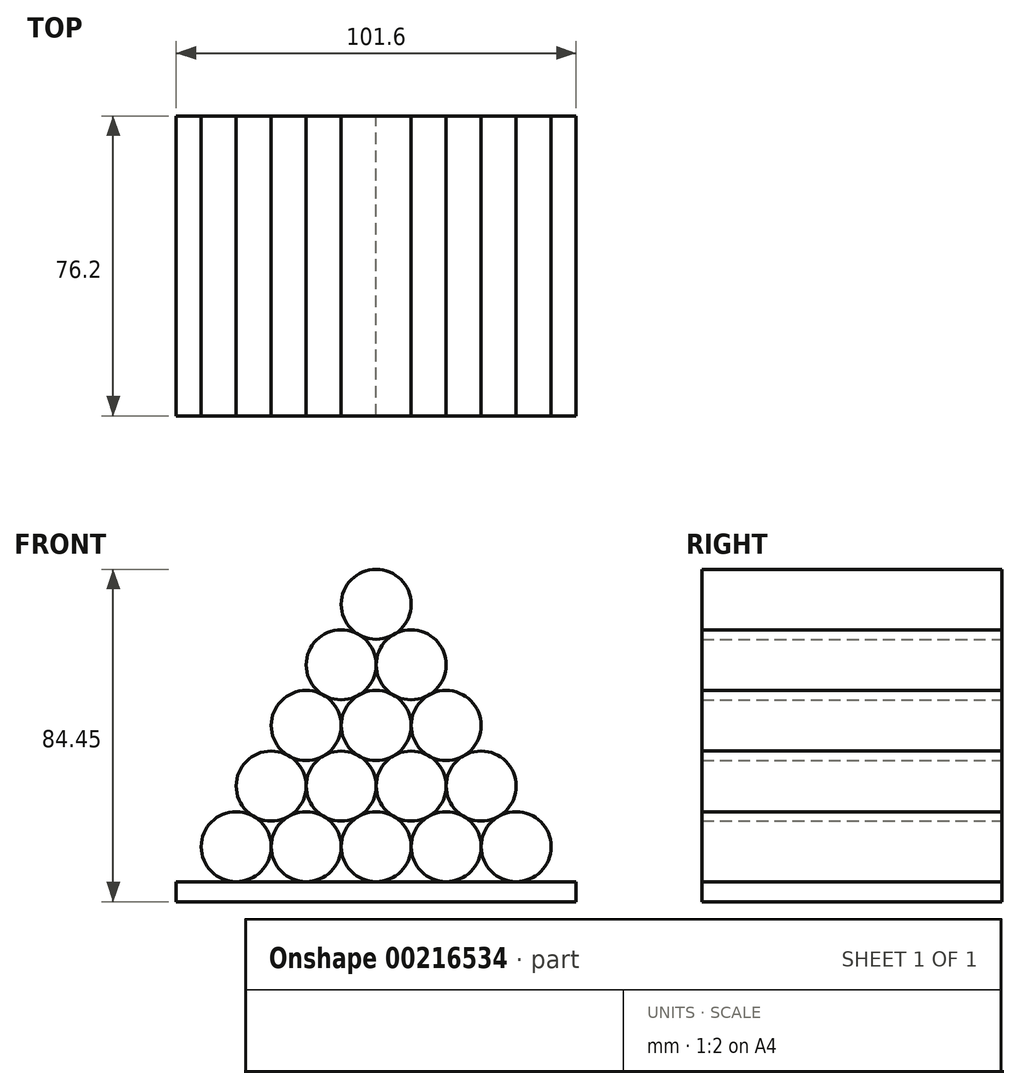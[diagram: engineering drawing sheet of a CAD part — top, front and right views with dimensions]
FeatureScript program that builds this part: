
annotation { "Feature Type Name" : "Feature", "Feature Type Description" : "" }
export const myFeature = defineFeature(function(context is Context, id is Id, definition is map)
    precondition{}
    {
        {
            var Q0;
            Q0=qCreatedBy(makeId("Front.planeOp"),FACE);
            var sketch = newSketch(context, id + "F0", { "sketchPlane" : qUnion([Q0])});
            skCircle(sketch, "E0", {"center": v(-26.67, 0) * mm, "radius": 8.9 * mm});
            skCircle(sketch, "E1", {"center": v(-8.9, 0) * mm, "radius": 8.9 * mm});
            skCircle(sketch, "E2", {"center": v(8.9, 0) * mm, "radius": 8.9 * mm});
            skCircle(sketch, "E3", {"center": v(26.67, 0) * mm, "radius": 8.9 * mm});
            skCircle(sketch, "E4", {"center": v(-17.78, 15.4) * mm, "radius": 8.9 * mm});
            skCircle(sketch, "E5", {"center": v(0, 15.4) * mm, "radius": 8.9 * mm});
            skCircle(sketch, "E6", {"center": v(17.78, 15.4) * mm, "radius": 8.9 * mm});
            skCircle(sketch, "E7", {"center": v(-35.56, -15.4) * mm, "radius": 8.9 * mm});
            skCircle(sketch, "E8", {"center": v(-17.78, -15.4) * mm, "radius": 8.9 * mm});
            skCircle(sketch, "E9", {"center": v(0, -15.4) * mm, "radius": 8.9 * mm});
            skCircle(sketch, "E10", {"center": v(17.78, -15.4) * mm, "radius": 8.9 * mm});
            skCircle(sketch, "E11", {"center": v(35.56, -15.4) * mm, "radius": 8.9 * mm});
            skLineSegment(sketch, "E12.bottom", {"start": v(-50.8, -24.29) * mm, "end": v(50.8, -24.29) * mm});
            skLineSegment(sketch, "E12.top", {"start": v(-50.8, -29.37) * mm, "end": v(50.8, -29.37) * mm});
            skLineSegment(sketch, "E12.left", {"start": v(-50.8, -24.29) * mm, "end": v(-50.8, -29.37) * mm});
            skLineSegment(sketch, "E12.right", {"start": v(50.8, -24.29) * mm, "end": v(50.8, -29.37) * mm});
            skCircle(sketch, "E13", {"center": v(-8.9, 30.8) * mm, "radius": 8.9 * mm});
            skCircle(sketch, "E14", {"center": v(8.89, 30.8) * mm, "radius": 8.9 * mm});
            skCircle(sketch, "E15", {"center": v(0, 46.2) * mm, "radius": 8.9 * mm});
            skSolve(sketch);
        }
        {
            var Q0;
            {var subQ0=sQuery(id+"F0.wireOp",EDGE,"E4");var subQ1=makeQuery(id+"F0.imprint","INTERSECT",VERTEX,{"derivedFrom":[sQuery(id+"F0.wireOp",EDGE,"E0"),subQ0]});Q0=makeQuery(id+"F0.imprint","IMPRINT",FACE,{"disambiguationData":[TD([[makeQuery(id+"F0.imprint","IMPRINT",EDGE,{"disambiguationData":[TD([[subQ1,1.0]])],"derivedFrom":subQ0}),1.0]])]});}
            var Q1;
            {var subQ0=sQuery(id+"F0.wireOp",EDGE,"E5");var subQ1=makeQuery(id+"F0.imprint","INTERSECT",VERTEX,{"derivedFrom":[sQuery(id+"F0.wireOp",EDGE,"E4"),subQ0]});Q1=makeQuery(id+"F0.imprint","IMPRINT",FACE,{"disambiguationData":[TD([[makeQuery(id+"F0.imprint","IMPRINT",EDGE,{"disambiguationData":[TD([[subQ1,1.0]])],"derivedFrom":subQ0}),1.0]])]});}
            var Q2;
            {var subQ0=sQuery(id+"F0.wireOp",EDGE,"E6");var subQ1=makeQuery(id+"F0.imprint","INTERSECT",VERTEX,{"derivedFrom":[sQuery(id+"F0.wireOp",EDGE,"E5"),subQ0]});Q2=makeQuery(id+"F0.imprint","IMPRINT",FACE,{"disambiguationData":[TD([[makeQuery(id+"F0.imprint","IMPRINT",EDGE,{"disambiguationData":[TD([[subQ1,-1.0]])],"derivedFrom":subQ0}),1.0]])]});}
            var Q3;
            {var subQ0=sQuery(id+"F0.wireOp",EDGE,"E3");var subQ1=makeQuery(id+"F0.imprint","INTERSECT",VERTEX,{"derivedFrom":[subQ0,sQuery(id+"F0.wireOp",EDGE,"E6")]});Q3=makeQuery(id+"F0.imprint","IMPRINT",FACE,{"disambiguationData":[TD([[makeQuery(id+"F0.imprint","IMPRINT",EDGE,{"disambiguationData":[TD([[subQ1,-1.0]])],"derivedFrom":subQ0}),1.0]])]});}
            var Q4;
            {var subQ0=sQuery(id+"F0.wireOp",EDGE,"E2");var subQ4=makeQuery(id+"F0.imprint","INTERSECT",VERTEX,{"derivedFrom":[subQ0,sQuery(id+"F0.wireOp",EDGE,"E6")]});Q4=makeQuery(id+"F0.imprint","IMPRINT",FACE,{"disambiguationData":[TD([[makeQuery(id+"F0.imprint","IMPRINT",EDGE,{"disambiguationData":[TD([[subQ4,1.0]])],"derivedFrom":subQ0}),1.0]])]});}
            var Q5;
            {var subQ0=sQuery(id+"F0.wireOp",EDGE,"E1");var subQ4=makeQuery(id+"F0.imprint","INTERSECT",VERTEX,{"derivedFrom":[subQ0,sQuery(id+"F0.wireOp",EDGE,"E5")]});Q5=makeQuery(id+"F0.imprint","IMPRINT",FACE,{"disambiguationData":[TD([[makeQuery(id+"F0.imprint","IMPRINT",EDGE,{"disambiguationData":[TD([[subQ4,1.0]])],"derivedFrom":subQ0}),1.0]])]});}
            var Q6;
            {var subQ0=sQuery(id+"F0.wireOp",EDGE,"E0");var subQ1=makeQuery(id+"F0.imprint","INTERSECT",VERTEX,{"derivedFrom":[subQ0,sQuery(id+"F0.wireOp",EDGE,"E4")]});Q6=makeQuery(id+"F0.imprint","IMPRINT",FACE,{"disambiguationData":[TD([[makeQuery(id+"F0.imprint","IMPRINT",EDGE,{"disambiguationData":[TD([[subQ1,1.0]])],"derivedFrom":subQ0}),1.0]])]});}
            var Q7;
            {var subQ0=sQuery(id+"F0.wireOp",EDGE,"E7");var subQ1=makeQuery(id+"F0.imprint","INTERSECT",VERTEX,{"derivedFrom":[sQuery(id+"F0.wireOp",EDGE,"E0"),subQ0]});Q7=makeQuery(id+"F0.imprint","IMPRINT",FACE,{"disambiguationData":[TD([[makeQuery(id+"F0.imprint","IMPRINT",EDGE,{"disambiguationData":[TD([[subQ1,1.0]])],"derivedFrom":subQ0}),1.0]])]});}
            var Q8;
            {var subQ0=sQuery(id+"F0.wireOp",EDGE,"E8");var subQ4=makeQuery(id+"F0.imprint","INTERSECT",VERTEX,{"derivedFrom":[sQuery(id+"F0.wireOp",EDGE,"E1"),subQ0]});Q8=makeQuery(id+"F0.imprint","IMPRINT",FACE,{"disambiguationData":[TD([[makeQuery(id+"F0.imprint","IMPRINT",EDGE,{"disambiguationData":[TD([[subQ4,1.0]])],"derivedFrom":subQ0}),1.0]])]});}
            var Q9;
            {var subQ0=sQuery(id+"F0.wireOp",EDGE,"E9");var subQ4=makeQuery(id+"F0.imprint","INTERSECT",VERTEX,{"derivedFrom":[sQuery(id+"F0.wireOp",EDGE,"E2"),subQ0]});Q9=makeQuery(id+"F0.imprint","IMPRINT",FACE,{"disambiguationData":[TD([[makeQuery(id+"F0.imprint","IMPRINT",EDGE,{"disambiguationData":[TD([[subQ4,1.0]])],"derivedFrom":subQ0}),1.0]])]});}
            var Q10;
            {var subQ0=sQuery(id+"F0.wireOp",EDGE,"E10");var subQ4=makeQuery(id+"F0.imprint","INTERSECT",VERTEX,{"derivedFrom":[sQuery(id+"F0.wireOp",EDGE,"E3"),subQ0]});Q10=makeQuery(id+"F0.imprint","IMPRINT",FACE,{"disambiguationData":[TD([[makeQuery(id+"F0.imprint","IMPRINT",EDGE,{"disambiguationData":[TD([[subQ4,1.0]])],"derivedFrom":subQ0}),1.0]])]});}
            var Q11;
            {var subQ0=sQuery(id+"F0.wireOp",EDGE,"E11");var subQ1=makeQuery(id+"F0.imprint","INTERSECT",VERTEX,{"derivedFrom":[sQuery(id+"F0.wireOp",EDGE,"E3"),subQ0]});Q11=makeQuery(id+"F0.imprint","IMPRINT",FACE,{"disambiguationData":[TD([[makeQuery(id+"F0.imprint","IMPRINT",EDGE,{"disambiguationData":[TD([[subQ1,-1.0]])],"derivedFrom":subQ0}),1.0]])]});}
            var Q12;
            Q12=makeQuery(id+"F0.imprint","IMPRINT",FACE,{"disambiguationData":[TD([[makeQuery(id+"F0.imprint","IMPRINT",EDGE,{"derivedFrom":sQuery(id+"F0.wireOp",EDGE,"E12.top")}),1.0]])]});
            var Q13;
            {var subQ0=sQuery(id+"F0.wireOp",EDGE,"E13");var subQ1=makeQuery(id+"F0.imprint","INTERSECT",VERTEX,{"derivedFrom":[subQ0,sQuery(id+"F0.wireOp",EDGE,"E15")]});Q13=makeQuery(id+"F0.imprint","IMPRINT",FACE,{"disambiguationData":[TD([[makeQuery(id+"F0.imprint","IMPRINT",EDGE,{"disambiguationData":[TD([[subQ1,1.0]])],"derivedFrom":subQ0}),1.0]])]});}
            var Q14;
            {var subQ0=sQuery(id+"F0.wireOp",EDGE,"E14");var subQ1=makeQuery(id+"F0.imprint","INTERSECT",VERTEX,{"derivedFrom":[subQ0,sQuery(id+"F0.wireOp",EDGE,"E15")]});Q14=makeQuery(id+"F0.imprint","IMPRINT",FACE,{"disambiguationData":[TD([[makeQuery(id+"F0.imprint","IMPRINT",EDGE,{"disambiguationData":[TD([[subQ1,-1.0]])],"derivedFrom":subQ0}),1.0]])]});}
            var Q15;
            {var subQ0=sQuery(id+"F0.wireOp",EDGE,"E15");var subQ1=makeQuery(id+"F0.imprint","INTERSECT",VERTEX,{"derivedFrom":[sQuery(id+"F0.wireOp",EDGE,"E13"),subQ0]});Q15=makeQuery(id+"F0.imprint","IMPRINT",FACE,{"disambiguationData":[TD([[makeQuery(id+"F0.imprint","IMPRINT",EDGE,{"disambiguationData":[TD([[subQ1,-1.0]])],"derivedFrom":subQ0}),1.0]])]});}
            var Q16;
            Q16=sQuery(id+"F0.wireOp",EDGE,"E5");
            var Q17;
            Q17=sQuery(id+"F0.wireOp",EDGE,"E6");
            var Q18;
            Q18=sQuery(id+"F0.wireOp",EDGE,"E12.bottom");
            var Q19;
            Q19=sQuery(id+"F0.wireOp",EDGE,"E1");
            var Q20;
            Q20=sQuery(id+"F0.wireOp",EDGE,"E3");
            var Q21;
            Q21=sQuery(id+"F0.wireOp",EDGE,"E4");
            var Q22;
            Q22=sQuery(id+"F0.wireOp",EDGE,"E11");
            var Q23;
            Q23=sQuery(id+"F0.wireOp",EDGE,"E8");
            var Q24;
            Q24=sQuery(id+"F0.wireOp",EDGE,"E2");
            var Q25;
            Q25=sQuery(id+"F0.wireOp",EDGE,"E12.top");
            var Q26;
            Q26=sQuery(id+"F0.wireOp",EDGE,"E0");
            var Q27;
            Q27=sQuery(id+"F0.wireOp",EDGE,"E9");
            var Q28;
            Q28=sQuery(id+"F0.wireOp",EDGE,"E10");
            var Q29;
            Q29=sQuery(id+"F0.wireOp",EDGE,"E7");
            var Q30;
            Q30=sQuery(id+"F0.wireOp",EDGE,"E12.left");
            var Q31;
            Q31=sQuery(id+"F0.wireOp",EDGE,"E12.right");
            extrude(context, id + "F1", {"entities" : qUnion([Q0, Q1, Q2, Q3, Q4, Q5, Q6, Q7, Q8, Q9, Q10, Q11, Q12, Q13, Q14, Q15]), "surfaceEntities" : qUnion([Q16, Q17, Q18, Q19, Q20, Q21, Q22, Q23, Q24, Q25, Q26, Q27, Q28, Q29, Q30, Q31]), "depth" : 76.2 * mm});
        }
    });
